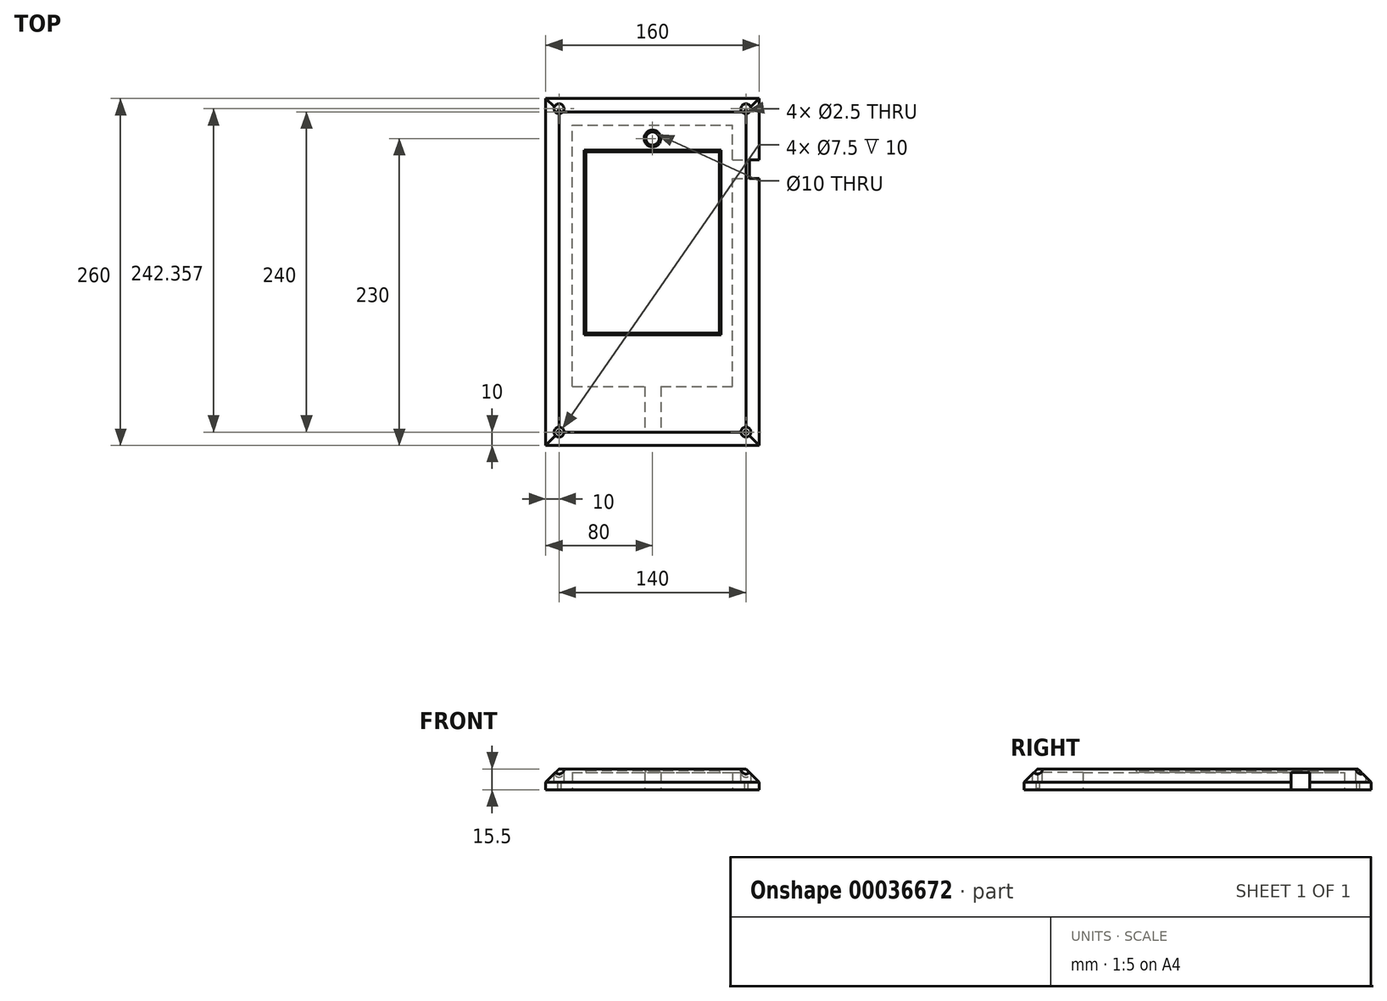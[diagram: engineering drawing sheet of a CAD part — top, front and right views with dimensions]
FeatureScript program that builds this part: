
annotation { "Feature Type Name" : "Feature", "Feature Type Description" : "" }
export const myFeature = defineFeature(function(context is Context, id is Id, definition is map)
    precondition{}
    {
        {
            var Q0;
            Q0=qCreatedBy(makeId("Top.planeOp"),FACE);
            var sketch = newSketch(context, id + "F0", { "sketchPlane" : qUnion([Q0])});
            skLineSegment(sketch, "E0.bottom", {"start": v(0, 0) * mm, "end": v(120, 0) * mm});
            skLineSegment(sketch, "E0.top", {"start": v(0, 196) * mm, "end": v(120, 196) * mm});
            skLineSegment(sketch, "E0.left", {"start": v(0, 0) * mm, "end": v(0, 196) * mm});
            skLineSegment(sketch, "E0.right", {"start": v(120, 0) * mm, "end": v(120, 196) * mm});
            skLineSegment(sketch, "E1.bottom", {"start": v(-20, 216) * mm, "end": v(140, 216) * mm});
            skLineSegment(sketch, "E1.top", {"start": v(-20, -44) * mm, "end": v(140, -44) * mm});
            skLineSegment(sketch, "E1.left", {"start": v(-20, 216) * mm, "end": v(-20, -44) * mm});
            skLineSegment(sketch, "E1.right", {"start": v(140, 216) * mm, "end": v(140, -44) * mm});
            skLineSegment(sketch, "E2.bottom", {"start": v(10, 176) * mm, "end": v(110, 176) * mm});
            skLineSegment(sketch, "E2.top", {"start": v(10, 40) * mm, "end": v(110, 40) * mm});
            skLineSegment(sketch, "E2.left", {"start": v(10, 178.5) * mm, "end": v(10, 40) * mm});
            skLineSegment(sketch, "E2.right", {"start": v(110, 176) * mm, "end": v(110, 40) * mm});
            skCircle(sketch, "E3", {"center": v(60, 186) * mm, "radius": 5 * mm});
            skCircle(sketch, "E4", {"center": v(-10, 206) * mm, "radius": 1.25 * mm});
            skCircle(sketch, "E5", {"center": v(-10, 206) * mm, "radius": 3.75 * mm});
            skCircle(sketch, "E6.1.0.0", {"center": v(130, 206) * mm, "radius": 3.75 * mm});
            skCircle(sketch, "E6.1.0.1", {"center": v(130, 206) * mm, "radius": 1.25 * mm});
            skLineSegment(sketch, "E6.direction1", {"start": v(-10, 206) * mm, "end": v(130, 206) * mm, "construction": true});
            skCircle(sketch, "E7.1.0.0", {"center": v(130, -34) * mm, "radius": 3.75 * mm});
            skCircle(sketch, "E7.1.0.1", {"center": v(-10, -34) * mm, "radius": 3.75 * mm});
            skLineSegment(sketch, "E7.direction1", {"start": v(130, 206) * mm, "end": v(130, -34) * mm, "construction": true});
            skCircle(sketch, "E8", {"center": v(-10, -34) * mm, "radius": 1.25 * mm});
            skCircle(sketch, "E9", {"center": v(130, -34) * mm, "radius": 1.25 * mm});
            skLineSegment(sketch, "E10.bottom", {"start": v(66, 0) * mm, "end": v(54, 0) * mm});
            skLineSegment(sketch, "E10.top", {"start": v(66, -44) * mm, "end": v(54, -44) * mm});
            skLineSegment(sketch, "E10.left", {"start": v(66, 0) * mm, "end": v(66, -44) * mm});
            skLineSegment(sketch, "E10.right", {"start": v(54, 0) * mm, "end": v(54, -44) * mm});
            skSolve(sketch);
        }
        {
            var Q0;
            Q0=makeQuery(id+"F0.imprint","IMPRINT",FACE,{"disambiguationData":[TD([[makeQuery(id+"F0.imprint","IMPRINT",EDGE,{"derivedFrom":sQuery(id+"F0.wireOp",EDGE,"E0.top")}),-1.0]])]});
            var Q1;
            Q1=makeQuery(id+"F0.imprint","IMPRINT",FACE,{"disambiguationData":[TD([[makeQuery(id+"F0.imprint","IMPRINT",EDGE,{"derivedFrom":sQuery(id+"F0.wireOp",EDGE,"E0.top")}),1.0]])]});
            var Q2;
            Q2=makeQuery(id+"F0.imprint","IMPRINT",FACE,{"disambiguationData":[TD([[makeQuery(id+"F0.imprint","IMPRINT",EDGE,{"derivedFrom":sQuery(id+"F0.wireOp",EDGE,"E7.1.0.0")}),1.0]])]});
            var Q3;
            Q3=makeQuery(id+"F0.imprint","IMPRINT",FACE,{"disambiguationData":[TD([[makeQuery(id+"F0.imprint","IMPRINT",EDGE,{"derivedFrom":sQuery(id+"F0.wireOp",EDGE,"E7.1.0.1")}),1.0]])]});
            var Q4;
            Q4=makeQuery(id+"F0.imprint","IMPRINT",FACE,{"disambiguationData":[TD([[makeQuery(id+"F0.imprint","IMPRINT",EDGE,{"derivedFrom":sQuery(id+"F0.wireOp",EDGE,"E4")}),-1.0]])]});
            var Q5;
            Q5=makeQuery(id+"F0.imprint","IMPRINT",FACE,{"disambiguationData":[TD([[makeQuery(id+"F0.imprint","IMPRINT",EDGE,{"derivedFrom":sQuery(id+"F0.wireOp",EDGE,"E6.1.0.0")}),1.0]])]});
            var Q6;
            {var subQ0=sQuery(id+"F0.wireOp",EDGE,"E10.left");Q6=makeQuery(id+"F0.imprint","IMPRINT",FACE,{"disambiguationData":[TD([[makeQuery(id+"F0.imprint","IMPRINT",EDGE,{"derivedFrom":subQ0}),-1.0]])]});}
            extrude(context, id + "F1", {"entities" : qUnion([Q0, Q1, Q2, Q3, Q4, Q5, Q6]), "depth" : 15.5 * mm});
        }
        {
            var Q0;
            Q0=makeQuery(id+"F0.imprint","IMPRINT",FACE,{"disambiguationData":[TD([[makeQuery(id+"F0.imprint","IMPRINT",EDGE,{"derivedFrom":sQuery(id+"F0.wireOp",EDGE,"E0.top")}),-1.0]])]});
            extrude(context, id + "F2", {"entities" : qUnion([Q0]), "operationType" : NewBodyOperationType.REMOVE, "depth" : 13 * mm});
        }
        {
            var Q0;
            Q0=makeQuery(id+"F1.opExtrude","CAP_FACE",FACE,{"disambiguationData":[OSD([sQuery(id+"F0.wireOp",EDGE,"E1.bottom"),sQuery(id+"F0.wireOp",EDGE,"E1.top"),sQuery(id+"F0.wireOp",EDGE,"E1.left"),sQuery(id+"F0.wireOp",EDGE,"E1.right"),sQuery(id+"F0.wireOp",EDGE,"E2.bottom"),sQuery(id+"F0.wireOp",EDGE,"E2.top"),sQuery(id+"F0.wireOp",EDGE,"E2.left"),sQuery(id+"F0.wireOp",EDGE,"E2.right"),sQuery(id+"F0.wireOp",EDGE,"E3"),sQuery(id+"F0.wireOp",EDGE,"E4"),sQuery(id+"F0.wireOp",EDGE,"E6.1.0.1"),sQuery(id+"F0.wireOp",EDGE,"E8"),sQuery(id+"F0.wireOp",EDGE,"E9")])],"isStart":false});
            cPlane(context, id + "F3", {"entities" : qUnion([Q0]), "cplaneType" : CPlaneType.OFFSET, "offset" : 0 * mm, "width" : 150 * mm, "height" : 150 * mm});
        }
        {
            var Q0;
            Q0=qCreatedBy(id+"F3.planeOp",FACE);
            var sketch = newSketch(context, id + "F4", { "sketchPlane" : qUnion([Q0])});
            skCircle(sketch, "E11.1.0.0", {"center": v(130, 208.36) * mm, "radius": 3.75 * mm});
            skCircle(sketch, "E12", {"center": v(-10, 208.36) * mm, "radius": 3.75 * mm});
            skCircle(sketch, "E13.1.0.0", {"center": v(130, -34) * mm, "radius": 3.75 * mm});
            skCircle(sketch, "E13.1.0.1", {"center": v(-10, -34) * mm, "radius": 3.75 * mm});
            skSolve(sketch);
        }
        {
            var Q0;
            Q0 = qSketchRegion(id + "F4", true);
            extrude(context, id + "F5", {"entities" : qUnion([Q0]), "operationType" : NewBodyOperationType.REMOVE, "oppositeDirection" : true, "depth" : 10 * mm});
        }
        {
            var Q0;
            Q0=makeQuery(id+"F1.opExtrude","CAP_EDGE",EDGE,{"disambiguationData":[OSD([sQuery(id+"F0.wireOp",EDGE,"E1.bottom")])],"isStart":false});
            var Q1;
            Q1=makeQuery(id+"F1.opExtrude","CAP_EDGE",EDGE,{"disambiguationData":[OSD([sQuery(id+"F0.wireOp",EDGE,"E1.right")])],"isStart":false});
            var Q2;
            Q2=makeQuery(id+"F1.opExtrude","CAP_EDGE",EDGE,{"disambiguationData":[OSD([sQuery(id+"F0.wireOp",EDGE,"E1.left")])],"isStart":false});
            var Q3;
            Q3=makeQuery(id+"F1.opExtrude","CAP_EDGE",EDGE,{"disambiguationData":[OSD([sQuery(id+"F0.wireOp",EDGE,"E1.top")])],"isStart":false});
            chamfer(context, id + "F6", {"entities" : qUnion([Q0, Q1, Q2, Q3]), "width" : 10 * mm, "tangentPropagation" : true});
        }
        {
            var Q0;
            Q0=makeQuery(id+"F1.opExtrude","CAP_EDGE",EDGE,{"disambiguationData":[OSD([sQuery(id+"F0.wireOp",EDGE,"E3")])],"isStart":false});
            chamfer(context, id + "F7", {"entities" : qUnion([Q0]), "width" : 1.25 * mm, "tangentPropagation" : true});
        }
        {
            var Q0;
            Q0=makeQuery(id+"F1.opExtrude","CAP_EDGE",EDGE,{"disambiguationData":[OSD([sQuery(id+"F0.wireOp",EDGE,"E2.right")])],"isStart":false});
            var Q1;
            Q1=makeQuery(id+"F1.opExtrude","CAP_EDGE",EDGE,{"disambiguationData":[OSD([sQuery(id+"F0.wireOp",EDGE,"E2.bottom")])],"isStart":false});
            var Q2;
            Q2=makeQuery(id+"F1.opExtrude","CAP_EDGE",EDGE,{"disambiguationData":[OSD([sQuery(id+"F0.wireOp",EDGE,"E2.left")])],"isStart":false});
            var Q3;
            Q3=makeQuery(id+"F1.opExtrude","CAP_EDGE",EDGE,{"disambiguationData":[OSD([sQuery(id+"F0.wireOp",EDGE,"E2.top")])],"isStart":false});
            chamfer(context, id + "F8", {"entities" : qUnion([Q0, Q1, Q2, Q3]), "width" : 1.25 * mm, "tangentPropagation" : true});
        }
        {
            var Q0;
            Q0=makeQuery(id+"F1.opExtrude","CAP_FACE",FACE,{"disambiguationData":[OSD([sQuery(id+"F0.wireOp",EDGE,"E1.bottom"),sQuery(id+"F0.wireOp",EDGE,"E1.top"),sQuery(id+"F0.wireOp",EDGE,"E1.left"),sQuery(id+"F0.wireOp",EDGE,"E1.right"),sQuery(id+"F0.wireOp",EDGE,"E2.bottom"),sQuery(id+"F0.wireOp",EDGE,"E2.top"),sQuery(id+"F0.wireOp",EDGE,"E2.left"),sQuery(id+"F0.wireOp",EDGE,"E2.right"),sQuery(id+"F0.wireOp",EDGE,"E3"),sQuery(id+"F0.wireOp",EDGE,"E4"),sQuery(id+"F0.wireOp",EDGE,"E6.1.0.1"),sQuery(id+"F0.wireOp",EDGE,"E8"),sQuery(id+"F0.wireOp",EDGE,"E9")])],"isStart":true});
            var sketch = newSketch(context, id + "F9", { "sketchPlane" : qUnion([Q0])});
            skLineSegment(sketch, "E14.bottom", {"start": v(66.33, 0) * mm, "end": v(54.33, 0) * mm});
            skLineSegment(sketch, "E14.top", {"start": v(66.33, 34) * mm, "end": v(54.33, 34) * mm});
            skLineSegment(sketch, "E14.left", {"start": v(66.33, 0) * mm, "end": v(66.33, 34) * mm});
            skLineSegment(sketch, "E14.right", {"start": v(54.33, 0) * mm, "end": v(54.33, 34) * mm});
            skLineSegment(sketch, "E15.bottom", {"start": v(120, -170) * mm, "end": v(140, -170) * mm});
            skLineSegment(sketch, "E15.top", {"start": v(120, -156) * mm, "end": v(140, -156) * mm});
            skLineSegment(sketch, "E15.left", {"start": v(120, -170) * mm, "end": v(120, -156) * mm});
            skLineSegment(sketch, "E15.right", {"start": v(140, -170) * mm, "end": v(140, -156) * mm});
            skSolve(sketch);
        }
        {
            var Q0;
            Q0 = qSketchRegion(id + "F9", true);
            extrude(context, id + "F10", {"entities" : qUnion([Q0]), "operationType" : NewBodyOperationType.REMOVE, "oppositeDirection" : true, "depth" : 13 * mm});
        }
    });
